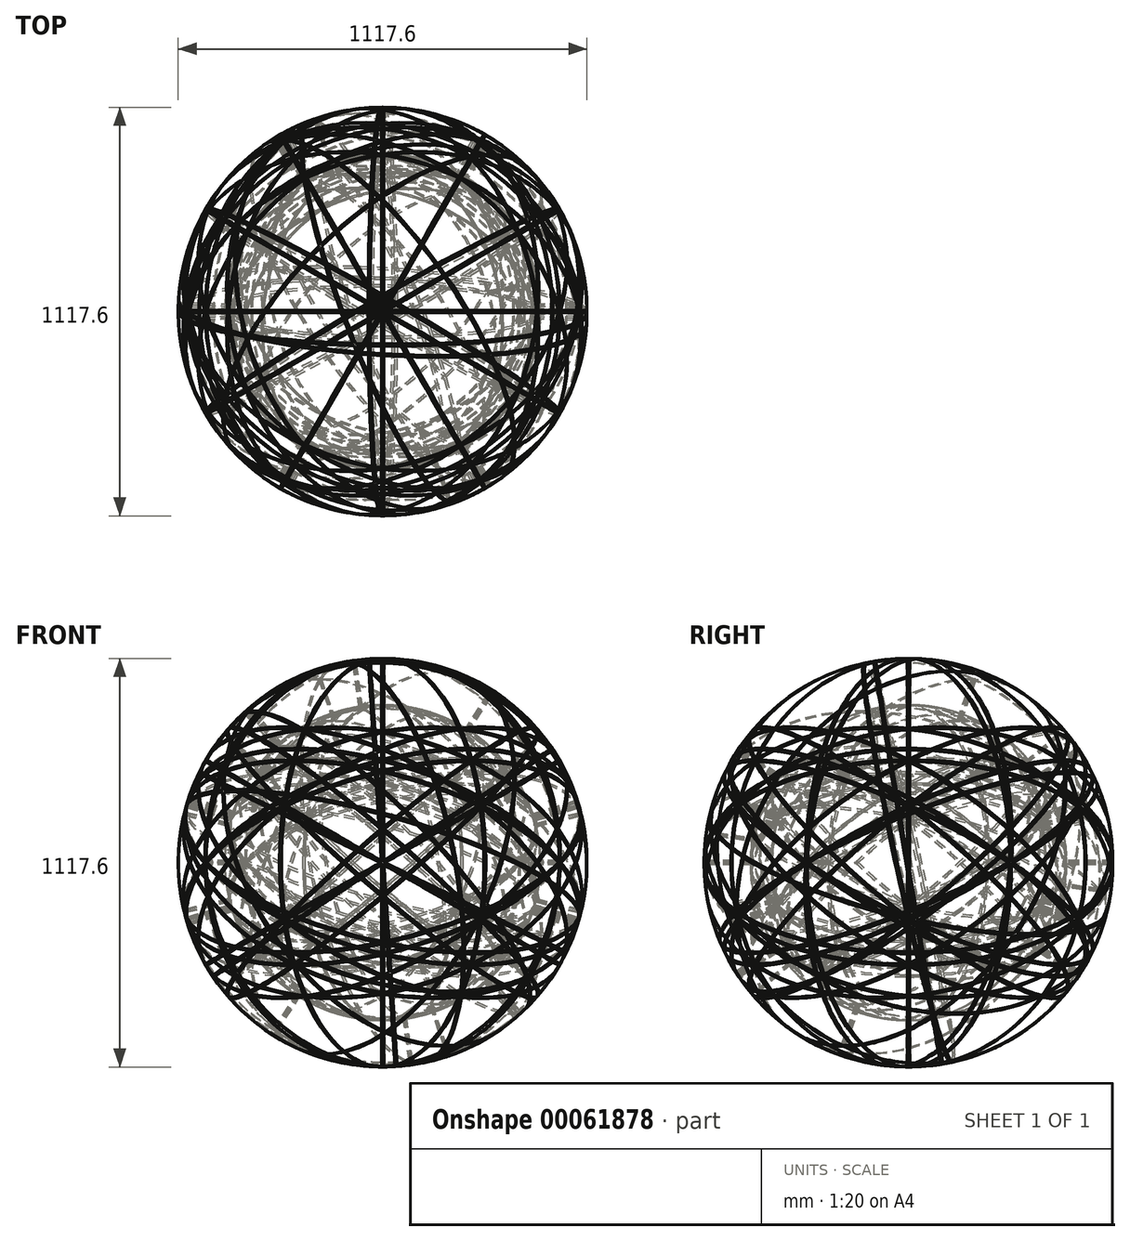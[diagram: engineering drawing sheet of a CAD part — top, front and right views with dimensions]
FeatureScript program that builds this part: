
annotation { "Feature Type Name" : "Feature", "Feature Type Description" : "" }
export const myFeature = defineFeature(function(context is Context, id is Id, definition is map)
    precondition{}
    {
        {
            var Q0;
            Q0=qCreatedBy(makeId("Front.planeOp"),FACE);
            var sketch = newSketch(context, id + "F0", { "sketchPlane" : qUnion([Q0])});
            skArc(sketch, "E0", {"start": v(0, 431.8) * mm, "mid": v(-431.8, 0) * mm, "end": v(0, -431.8) * mm});
            skArc(sketch, "E1", {"start": v(0, 558.8) * mm, "mid": v(-558.8, 0) * mm, "end": v(0, -558.8) * mm});
            skLineSegment(sketch, "E2", {"start": v(0, -558.8) * mm, "end": v(0, 558.8) * mm, "construction": true});
            skLineSegment(sketch, "E3", {"start": v(0, 558.8) * mm, "end": v(0, 431.8) * mm});
            skLineSegment(sketch, "E4", {"start": v(0, -558.8) * mm, "end": v(0, -431.8) * mm});
            skSolve(sketch);
        }
        {
            var Q0;
            Q0 = qSketchRegion(id + "F0", true);
            var Q1;
            Q1=sQuery(id+"F0.wireOp",EDGE,"E2");
            revolve(context, id + "F1", {"entities" : qUnion([Q0]), "axis" : qUnion([Q1]), "revolveType" : RevolveType.FULL});
        }
        {
            var Q0;
            Q0=qCreatedBy(makeId("Front.planeOp"),FACE);
            var sketch = newSketch(context, id + "F2", { "sketchPlane" : qUnion([Q0])});
            skLineSegment(sketch, "E5", {"start": v(0, 772.8) * mm, "end": v(0, 0) * mm});
            skLineSegment(sketch, "E6", {"start": v(0, 0) * mm, "end": v(0, -862.47) * mm});
            skLineSegment(sketch, "E7", {"start": v(772.58, 517.2) * mm, "end": v(0, 0) * mm});
            skLineSegment(sketch, "E8", {"start": v(0, 0) * mm, "end": v(-797.79, -534.07) * mm});
            skLineSegment(sketch, "E9.0", {"start": v(-3.17, 1.7) * mm, "end": v(-799.55, -531.43) * mm});
            skLineSegment(sketch, "E9.1", {"start": v(-3.18, 772.8) * mm, "end": v(-3.18, 1.7) * mm});
            skLineSegment(sketch, "E10.0", {"start": v(-3.17, -5.95) * mm, "end": v(-786.88, -530.6) * mm});
            skLineSegment(sketch, "E10.1", {"start": v(-3.17, -5.95) * mm, "end": v(-3.17, -862.47) * mm});
            skLineSegment(sketch, "E11.0", {"start": v(3.18, -1.7) * mm, "end": v(3.18, -862.47) * mm});
            skLineSegment(sketch, "E11.1", {"start": v(783.48, 520.67) * mm, "end": v(3.17, -1.7) * mm});
            skLineSegment(sketch, "E12.0", {"start": v(3.17, 772.8) * mm, "end": v(3.18, 5.95) * mm});
            skLineSegment(sketch, "E12.1", {"start": v(770.8, 519.83) * mm, "end": v(3.17, 5.95) * mm});
            skLineSegment(sketch, "E13", {"start": v(-3.18, 772.8) * mm, "end": v(3.17, 772.8) * mm});
            skLineSegment(sketch, "E14", {"start": v(770.8, 519.83) * mm, "end": v(783.48, 520.67) * mm});
            skLineSegment(sketch, "E15", {"start": v(3.18, -862.47) * mm, "end": v(-3.17, -862.47) * mm});
            skLineSegment(sketch, "E16", {"start": v(-786.88, -530.6) * mm, "end": v(-799.55, -531.43) * mm});
            skSolve(sketch);
        }
        {
            var Q0;
            Q0 = qSketchRegion(id + "F2", true);
            extrude(context, id + "F3", {"entities" : qUnion([Q0]), "operationType" : NewBodyOperationType.REMOVE, "endBound" : BoundingType.THROUGH_ALL, "oppositeDirection" : true, "depth" : 25.4 * mm, "hasSecondDirection" : true, "secondDirectionBound" : SecondDirectionBoundingType.THROUGH_ALL, "secondDirectionOppositeDirection" : false, "secondDirectionDepth" : 25.4 * mm});
        }
        {
            var Q0;
            Q0=qCreatedBy(makeId("Front.planeOp"),FACE);
            var sketch = newSketch(context, id + "F4", { "sketchPlane" : qUnion([Q0])});
            skLineSegment(sketch, "E17", {"start": v(0, 0) * mm, "end": v(409.24, 708.83) * mm});
            skLineSegment(sketch, "E18", {"start": v(409.24, 708.83) * mm, "end": v(0, 708.83) * mm});
            skLineSegment(sketch, "E19", {"start": v(0, 708.83) * mm, "end": v(0, 0) * mm});
            skSolve(sketch);
        }
        {
            var Q0;
            Q0=qCreatedBy(makeId("Top.planeOp"),FACE);
            var sketch = newSketch(context, id + "F5", { "sketchPlane" : qUnion([Q0])});
            skLineSegment(sketch, "E20", {"start": v(0, 0) * mm, "end": v(0, -768.93) * mm});
            skSolve(sketch);
        }
        {
            var Q0;
            Q0=sQuery(id+"F5.wireOp",VERTEX,"E20.end");
            var Q1;
            Q1=sQuery(id+"F5.wireOp",VERTEX,"E20.start");
            var Q2;
            Q2=sQuery(id+"F4.wireOp",VERTEX,"E18.start");
            cPlane(context, id + "F6", {"entities" : qUnion([Q0, Q1, Q2]), "cplaneType" : CPlaneType.THREE_POINT, "offset" : 152.4 * mm, "width" : 152.4 * mm, "height" : 152.4 * mm});
        }
        {
            var Q0;
            Q0=qCreatedBy(id+"F6.planeOp",FACE);
            var sketch = newSketch(context, id + "F7", { "sketchPlane" : qUnion([Q0])});
            skLineSegment(sketch, "E21", {"start": v(0, 0) * mm, "end": v(714.18, 412.33) * mm});
            skLineSegment(sketch, "E22", {"start": v(0, 0) * mm, "end": v(1115.7, 0) * mm});
            skLineSegment(sketch, "E23.0", {"start": v(1.59, -2.75) * mm, "end": v(715.77, 409.58) * mm});
            skLineSegment(sketch, "E24.0", {"start": v(-1.59, 2.75) * mm, "end": v(712.6, 415.08) * mm});
            skLineSegment(sketch, "E25", {"start": v(715.77, 409.58) * mm, "end": v(712.6, 415.08) * mm});
            skLineSegment(sketch, "E26", {"start": v(1.59, -2.75) * mm, "end": v(-1.59, 2.75) * mm});
            skLineSegment(sketch, "E27.MirrorCS", {"start": v(1.59, -2.75) * mm, "end": v(-712.6, -415.08) * mm});
            skLineSegment(sketch, "E28.MirrorCS", {"start": v(-1.59, 2.75) * mm, "end": v(-715.77, -409.58) * mm});
            skLineSegment(sketch, "E29.MirrorCS", {"start": v(-712.6, -415.08) * mm, "end": v(-715.77, -409.58) * mm});
            skLineSegment(sketch, "E30", {"start": v(0, 0) * mm, "end": v(-803.14, 0) * mm, "construction": true});
            skLineSegment(sketch, "E31.MirrorCS", {"start": v(-712.6, 415.08) * mm, "end": v(-715.77, 409.58) * mm});
            skLineSegment(sketch, "E32.MirrorCS", {"start": v(-1.59, -2.75) * mm, "end": v(-715.77, 409.58) * mm});
            skLineSegment(sketch, "E33.MirrorCS", {"start": v(1.59, 2.75) * mm, "end": v(-712.6, 415.08) * mm});
            skLineSegment(sketch, "E34.MirrorCS", {"start": v(715.77, -409.58) * mm, "end": v(712.6, -415.08) * mm});
            skLineSegment(sketch, "E35.MirrorCS", {"start": v(1.59, 2.75) * mm, "end": v(715.77, -409.58) * mm});
            skLineSegment(sketch, "E36.MirrorCS", {"start": v(0, 0) * mm, "end": v(714.18, -412.33) * mm});
            skLineSegment(sketch, "E37.MirrorCS", {"start": v(-1.59, -2.75) * mm, "end": v(712.6, -415.08) * mm});
            skSolve(sketch);
        }
        {
            var Q0;
            Q0 = qSketchRegion(id + "F7", true);
            extrude(context, id + "F8", {"entities" : qUnion([Q0]), "operationType" : NewBodyOperationType.REMOVE, "endBound" : BoundingType.THROUGH_ALL, "oppositeDirection" : true, "depth" : 25.4 * mm, "hasSecondDirection" : true, "secondDirectionBound" : SecondDirectionBoundingType.THROUGH_ALL, "secondDirectionOppositeDirection" : false, "secondDirectionDepth" : 25.4 * mm});
        }
        {
            var Q0;
            Q0=makeQuery(id+"F8.boolean.opBoolean","SPLIT",BODY,{"disambiguationData":[OD(1.0)],"derivedFrom":makeQuery(id+"F3.boolean.opBoolean","SPLIT",BODY,{"disambiguationData":[OD(1.0)],"derivedFrom":makeQuery(id+"F1.opRevolve","SWEPT_BODY",BODY,{"disambiguationData":[OSD([sQuery(id+"F0.wireOp",EDGE,"E0"),sQuery(id+"F0.wireOp",EDGE,"E1"),sQuery(id+"F0.wireOp",EDGE,"E3"),sQuery(id+"F0.wireOp",EDGE,"E4")])]})})});
            var Q1;
            Q1=makeQuery(id+"F8.boolean.opBoolean","SPLIT",BODY,{"disambiguationData":[OD(1.0)],"derivedFrom":makeQuery(id+"F3.boolean.opBoolean","SPLIT",BODY,{"disambiguationData":[OD(3.0)],"derivedFrom":makeQuery(id+"F1.opRevolve","SWEPT_BODY",BODY,{"disambiguationData":[OSD([sQuery(id+"F0.wireOp",EDGE,"E0"),sQuery(id+"F0.wireOp",EDGE,"E1"),sQuery(id+"F0.wireOp",EDGE,"E3"),sQuery(id+"F0.wireOp",EDGE,"E4")])]})})});
            var Q2;
            Q2=makeQuery(id+"F8.boolean.opBoolean","SPLIT",BODY,{"disambiguationData":[OD(2.0)],"derivedFrom":makeQuery(id+"F3.boolean.opBoolean","SPLIT",BODY,{"disambiguationData":[OD(1.0)],"derivedFrom":makeQuery(id+"F1.opRevolve","SWEPT_BODY",BODY,{"disambiguationData":[OSD([sQuery(id+"F0.wireOp",EDGE,"E0"),sQuery(id+"F0.wireOp",EDGE,"E1"),sQuery(id+"F0.wireOp",EDGE,"E3"),sQuery(id+"F0.wireOp",EDGE,"E4")])]})})});
            var Q3;
            Q3=makeQuery(id+"F8.boolean.opBoolean","SPLIT",BODY,{"disambiguationData":[OD(2.0)],"derivedFrom":makeQuery(id+"F3.boolean.opBoolean","SPLIT",BODY,{"disambiguationData":[OD(3.0)],"derivedFrom":makeQuery(id+"F1.opRevolve","SWEPT_BODY",BODY,{"disambiguationData":[OSD([sQuery(id+"F0.wireOp",EDGE,"E0"),sQuery(id+"F0.wireOp",EDGE,"E1"),sQuery(id+"F0.wireOp",EDGE,"E3"),sQuery(id+"F0.wireOp",EDGE,"E4")])]})})});
            var Q4;
            Q4=sQuery(id+"F5.wireOp",EDGE,"E20");
            circularPattern(context, id + "F9", {"entities" : qUnion([Q0, Q1, Q2, Q3]), "axis" : qUnion([Q4]), "angle" : 60 * degree, "instanceCount" : 3});
        }
        {
            var Q0;
            Q0=makeQuery(id+"F8.boolean.opBoolean","SPLIT",BODY,{"disambiguationData":[OD(2.0)],"derivedFrom":makeQuery(id+"F3.boolean.opBoolean","SPLIT",BODY,{"disambiguationData":[OD(1.0)],"derivedFrom":makeQuery(id+"F1.opRevolve","SWEPT_BODY",BODY,{"disambiguationData":[OSD([sQuery(id+"F0.wireOp",EDGE,"E0"),sQuery(id+"F0.wireOp",EDGE,"E1"),sQuery(id+"F0.wireOp",EDGE,"E3"),sQuery(id+"F0.wireOp",EDGE,"E4")])]})})});
            var Q1;
            Q1=makeQuery(id+"F9.opPattern","COPY",BODY,{"derivedFrom":makeQuery(id+"F8.boolean.opBoolean","SPLIT",BODY,{"disambiguationData":[OD(2.0)],"derivedFrom":makeQuery(id+"F3.boolean.opBoolean","SPLIT",BODY,{"disambiguationData":[OD(3.0)],"derivedFrom":makeQuery(id+"F1.opRevolve","SWEPT_BODY",BODY,{"disambiguationData":[OSD([sQuery(id+"F0.wireOp",EDGE,"E0"),sQuery(id+"F0.wireOp",EDGE,"E1"),sQuery(id+"F0.wireOp",EDGE,"E3"),sQuery(id+"F0.wireOp",EDGE,"E4")])]})})}),"instanceName":"2"});
            var Q2;
            Q2=makeQuery(id+"F9.opPattern","COPY",BODY,{"derivedFrom":makeQuery(id+"F8.boolean.opBoolean","SPLIT",BODY,{"disambiguationData":[OD(2.0)],"derivedFrom":makeQuery(id+"F3.boolean.opBoolean","SPLIT",BODY,{"disambiguationData":[OD(3.0)],"derivedFrom":makeQuery(id+"F1.opRevolve","SWEPT_BODY",BODY,{"disambiguationData":[OSD([sQuery(id+"F0.wireOp",EDGE,"E0"),sQuery(id+"F0.wireOp",EDGE,"E1"),sQuery(id+"F0.wireOp",EDGE,"E3"),sQuery(id+"F0.wireOp",EDGE,"E4")])]})})}),"instanceName":"1"});
            var Q3;
            Q3=makeQuery(id+"F8.boolean.opBoolean","SPLIT",BODY,{"disambiguationData":[OD(2.0)],"derivedFrom":makeQuery(id+"F3.boolean.opBoolean","SPLIT",BODY,{"disambiguationData":[OD(3.0)],"derivedFrom":makeQuery(id+"F1.opRevolve","SWEPT_BODY",BODY,{"disambiguationData":[OSD([sQuery(id+"F0.wireOp",EDGE,"E0"),sQuery(id+"F0.wireOp",EDGE,"E1"),sQuery(id+"F0.wireOp",EDGE,"E3"),sQuery(id+"F0.wireOp",EDGE,"E4")])]})})});
            var Q4;
            Q4=makeQuery(id+"F9.opPattern","COPY",BODY,{"derivedFrom":makeQuery(id+"F8.boolean.opBoolean","SPLIT",BODY,{"disambiguationData":[OD(2.0)],"derivedFrom":makeQuery(id+"F3.boolean.opBoolean","SPLIT",BODY,{"disambiguationData":[OD(1.0)],"derivedFrom":makeQuery(id+"F1.opRevolve","SWEPT_BODY",BODY,{"disambiguationData":[OSD([sQuery(id+"F0.wireOp",EDGE,"E0"),sQuery(id+"F0.wireOp",EDGE,"E1"),sQuery(id+"F0.wireOp",EDGE,"E3"),sQuery(id+"F0.wireOp",EDGE,"E4")])]})})}),"instanceName":"2"});
            var Q5;
            Q5=makeQuery(id+"F9.opPattern","COPY",BODY,{"derivedFrom":makeQuery(id+"F8.boolean.opBoolean","SPLIT",BODY,{"disambiguationData":[OD(2.0)],"derivedFrom":makeQuery(id+"F3.boolean.opBoolean","SPLIT",BODY,{"disambiguationData":[OD(1.0)],"derivedFrom":makeQuery(id+"F1.opRevolve","SWEPT_BODY",BODY,{"disambiguationData":[OSD([sQuery(id+"F0.wireOp",EDGE,"E0"),sQuery(id+"F0.wireOp",EDGE,"E1"),sQuery(id+"F0.wireOp",EDGE,"E3"),sQuery(id+"F0.wireOp",EDGE,"E4")])]})})}),"instanceName":"1"});
            var Q6;
            Q6=makeQuery(id+"F9.opPattern","COPY",BODY,{"derivedFrom":makeQuery(id+"F8.boolean.opBoolean","SPLIT",BODY,{"disambiguationData":[OD(1.0)],"derivedFrom":makeQuery(id+"F3.boolean.opBoolean","SPLIT",BODY,{"disambiguationData":[OD(3.0)],"derivedFrom":makeQuery(id+"F1.opRevolve","SWEPT_BODY",BODY,{"disambiguationData":[OSD([sQuery(id+"F0.wireOp",EDGE,"E0"),sQuery(id+"F0.wireOp",EDGE,"E1"),sQuery(id+"F0.wireOp",EDGE,"E3"),sQuery(id+"F0.wireOp",EDGE,"E4")])]})})}),"instanceName":"1"});
            var Q7;
            Q7=makeQuery(id+"F9.opPattern","COPY",BODY,{"derivedFrom":makeQuery(id+"F8.boolean.opBoolean","SPLIT",BODY,{"disambiguationData":[OD(1.0)],"derivedFrom":makeQuery(id+"F3.boolean.opBoolean","SPLIT",BODY,{"disambiguationData":[OD(3.0)],"derivedFrom":makeQuery(id+"F1.opRevolve","SWEPT_BODY",BODY,{"disambiguationData":[OSD([sQuery(id+"F0.wireOp",EDGE,"E0"),sQuery(id+"F0.wireOp",EDGE,"E1"),sQuery(id+"F0.wireOp",EDGE,"E3"),sQuery(id+"F0.wireOp",EDGE,"E4")])]})})}),"instanceName":"2"});
            var Q8;
            Q8=makeQuery(id+"F8.boolean.opBoolean","SPLIT",BODY,{"disambiguationData":[OD(1.0)],"derivedFrom":makeQuery(id+"F3.boolean.opBoolean","SPLIT",BODY,{"disambiguationData":[OD(1.0)],"derivedFrom":makeQuery(id+"F1.opRevolve","SWEPT_BODY",BODY,{"disambiguationData":[OSD([sQuery(id+"F0.wireOp",EDGE,"E0"),sQuery(id+"F0.wireOp",EDGE,"E1"),sQuery(id+"F0.wireOp",EDGE,"E3"),sQuery(id+"F0.wireOp",EDGE,"E4")])]})})});
            var Q9;
            Q9=makeQuery(id+"F9.opPattern","COPY",BODY,{"derivedFrom":makeQuery(id+"F8.boolean.opBoolean","SPLIT",BODY,{"disambiguationData":[OD(1.0)],"derivedFrom":makeQuery(id+"F3.boolean.opBoolean","SPLIT",BODY,{"disambiguationData":[OD(1.0)],"derivedFrom":makeQuery(id+"F1.opRevolve","SWEPT_BODY",BODY,{"disambiguationData":[OSD([sQuery(id+"F0.wireOp",EDGE,"E0"),sQuery(id+"F0.wireOp",EDGE,"E1"),sQuery(id+"F0.wireOp",EDGE,"E3"),sQuery(id+"F0.wireOp",EDGE,"E4")])]})})}),"instanceName":"1"});
            var Q10;
            Q10=makeQuery(id+"F9.opPattern","COPY",BODY,{"derivedFrom":makeQuery(id+"F8.boolean.opBoolean","SPLIT",BODY,{"disambiguationData":[OD(1.0)],"derivedFrom":makeQuery(id+"F3.boolean.opBoolean","SPLIT",BODY,{"disambiguationData":[OD(1.0)],"derivedFrom":makeQuery(id+"F1.opRevolve","SWEPT_BODY",BODY,{"disambiguationData":[OSD([sQuery(id+"F0.wireOp",EDGE,"E0"),sQuery(id+"F0.wireOp",EDGE,"E1"),sQuery(id+"F0.wireOp",EDGE,"E3"),sQuery(id+"F0.wireOp",EDGE,"E4")])]})})}),"instanceName":"2"});
            var Q11;
            Q11=makeQuery(id+"F8.boolean.opBoolean","SPLIT",BODY,{"disambiguationData":[OD(1.0)],"derivedFrom":makeQuery(id+"F3.boolean.opBoolean","SPLIT",BODY,{"disambiguationData":[OD(3.0)],"derivedFrom":makeQuery(id+"F1.opRevolve","SWEPT_BODY",BODY,{"disambiguationData":[OSD([sQuery(id+"F0.wireOp",EDGE,"E0"),sQuery(id+"F0.wireOp",EDGE,"E1"),sQuery(id+"F0.wireOp",EDGE,"E3"),sQuery(id+"F0.wireOp",EDGE,"E4")])]})})});
            var Q12;
            Q12=sQuery(id+"F4.wireOp",EDGE,"E19");
            circularPattern(context, id + "F10", {"entities" : qUnion([Q0, Q1, Q2, Q3, Q4, Q5, Q6, Q7, Q8, Q9, Q10, Q11]), "axis" : qUnion([Q12]), "angle" : 60 * degree, "instanceCount" : 3});
        }
        {
            var Q0;
            Q0=qCreatedBy(makeId("Front.planeOp"),FACE);
            var sketch = newSketch(context, id + "F11", { "sketchPlane" : qUnion([Q0])});
            skLineSegment(sketch, "E38", {"start": v(0, 0) * mm, "end": v(0, 835.47) * mm});
            skLineSegment(sketch, "E39", {"start": v(0, 835.47) * mm, "end": v(-886.09, 254.08) * mm});
            skLineSegment(sketch, "E40", {"start": v(-886.09, 254.08) * mm, "end": v(0, 0) * mm});
            skSolve(sketch);
        }
        {
            var Q0;
            Q0=makeQuery(id+"F10.opPattern","COPY",BODY,{"derivedFrom":makeQuery(id+"F8.boolean.opBoolean","SPLIT",BODY,{"disambiguationData":[OD(1.0)],"derivedFrom":makeQuery(id+"F3.boolean.opBoolean","SPLIT",BODY,{"disambiguationData":[OD(3.0)],"derivedFrom":makeQuery(id+"F1.opRevolve","SWEPT_BODY",BODY,{"disambiguationData":[OSD([sQuery(id+"F0.wireOp",EDGE,"E0"),sQuery(id+"F0.wireOp",EDGE,"E1"),sQuery(id+"F0.wireOp",EDGE,"E3"),sQuery(id+"F0.wireOp",EDGE,"E4")])]})})}),"instanceName":"2"});
            var Q1;
            Q1=sQuery(id+"F11.wireOp",EDGE,"E40");
            circularPattern(context, id + "F12", {"entities" : qUnion([Q0]), "axis" : qUnion([Q1]), "angle" : 64 * degree, "instanceCount" : 3});
        }
    });
